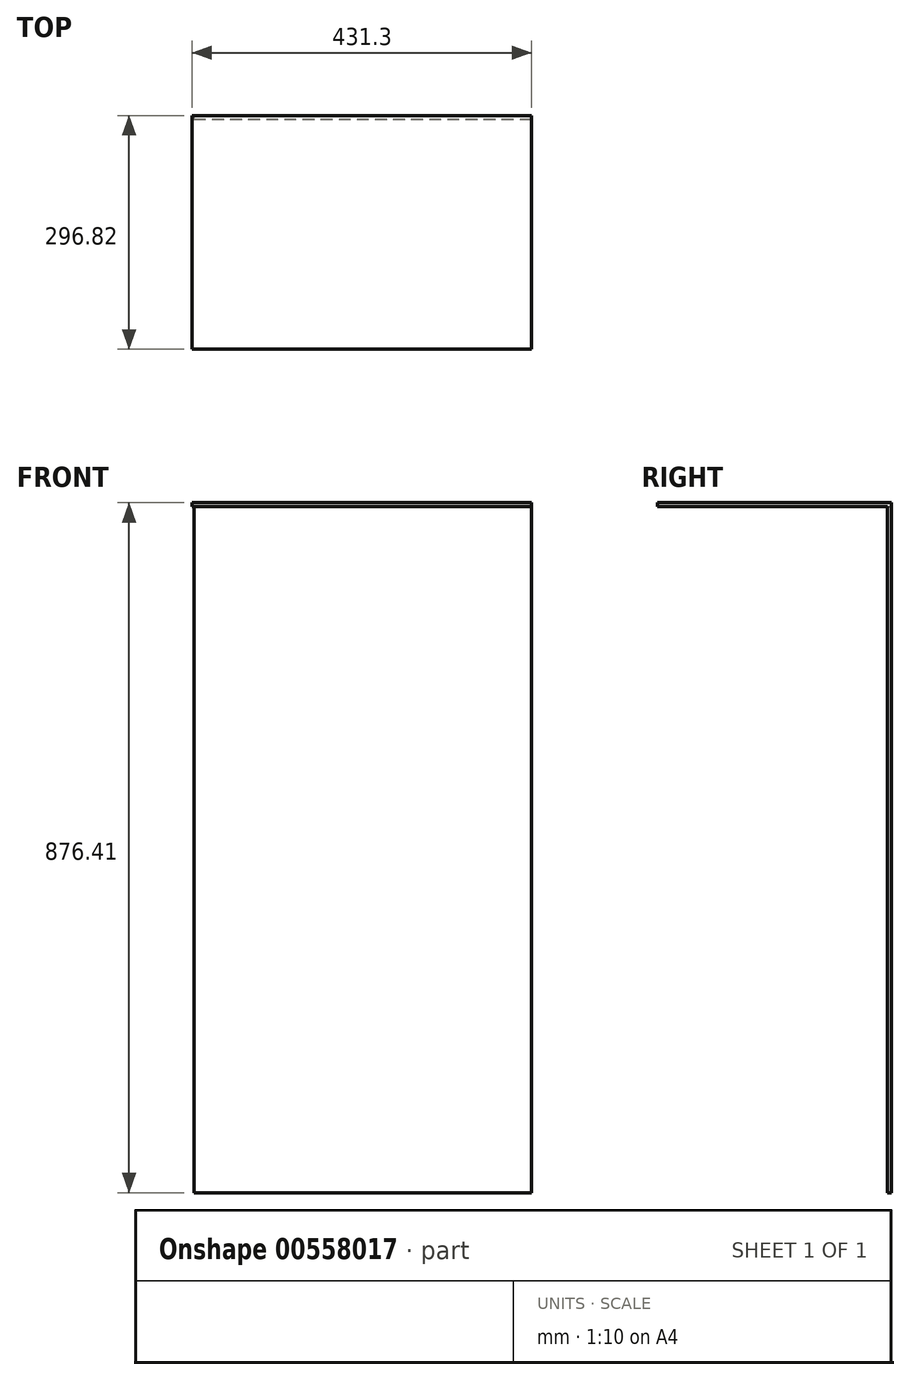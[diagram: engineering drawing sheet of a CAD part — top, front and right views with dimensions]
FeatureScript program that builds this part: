
annotation { "Feature Type Name" : "Feature", "Feature Type Description" : "" }
export const myFeature = defineFeature(function(context is Context, id is Id, definition is map)
    precondition{}
    {
        {
            var Q0;
            Q0=qCreatedBy(makeId("Front.planeOp"),FACE);
            var sketch = newSketch(context, id + "F0", { "sketchPlane" : qUnion([Q0])});
            skLineSegment(sketch, "E0.bottom", {"start": v(0, 0) * mm, "end": v(-429.03, 0) * mm});
            skLineSegment(sketch, "E0.top", {"start": v(0, -871.33) * mm, "end": v(-429.03, -871.33) * mm});
            skLineSegment(sketch, "E0.left", {"start": v(0, 0) * mm, "end": v(0, -871.33) * mm});
            skLineSegment(sketch, "E0.right", {"start": v(-429.03, 0) * mm, "end": v(-429.03, -871.33) * mm});
            skSolve(sketch);
        }
        {
            var Q0;
            Q0 = qSketchRegion(id + "F0", true);
            extrude(context, id + "F1", {"entities" : qUnion([Q0]), "depth" : 5.08 * mm, "offsetDistance" : 25.4 * mm});
        }
        {
            var Q0;
            Q0=qCreatedBy(makeId("Top.planeOp"),FACE);
            var sketch = newSketch(context, id + "F2", { "sketchPlane" : qUnion([Q0])});
            skLineSegment(sketch, "E1.bottom", {"start": v(0, 0) * mm, "end": v(-431.3, 0) * mm});
            skLineSegment(sketch, "E1.top", {"start": v(0, -296.82) * mm, "end": v(-431.3, -296.82) * mm});
            skLineSegment(sketch, "E1.left", {"start": v(0, 0) * mm, "end": v(0, -296.82) * mm});
            skLineSegment(sketch, "E1.right", {"start": v(-431.3, 0) * mm, "end": v(-431.3, -296.82) * mm});
            skSolve(sketch);
        }
        {
            var Q0;
            Q0 = qSketchRegion(id + "F2", true);
            extrude(context, id + "F3", {"entities" : qUnion([Q0]), "operationType" : NewBodyOperationType.ADD, "depth" : 5.08 * mm, "offsetDistance" : 25.4 * mm});
        }
    });
